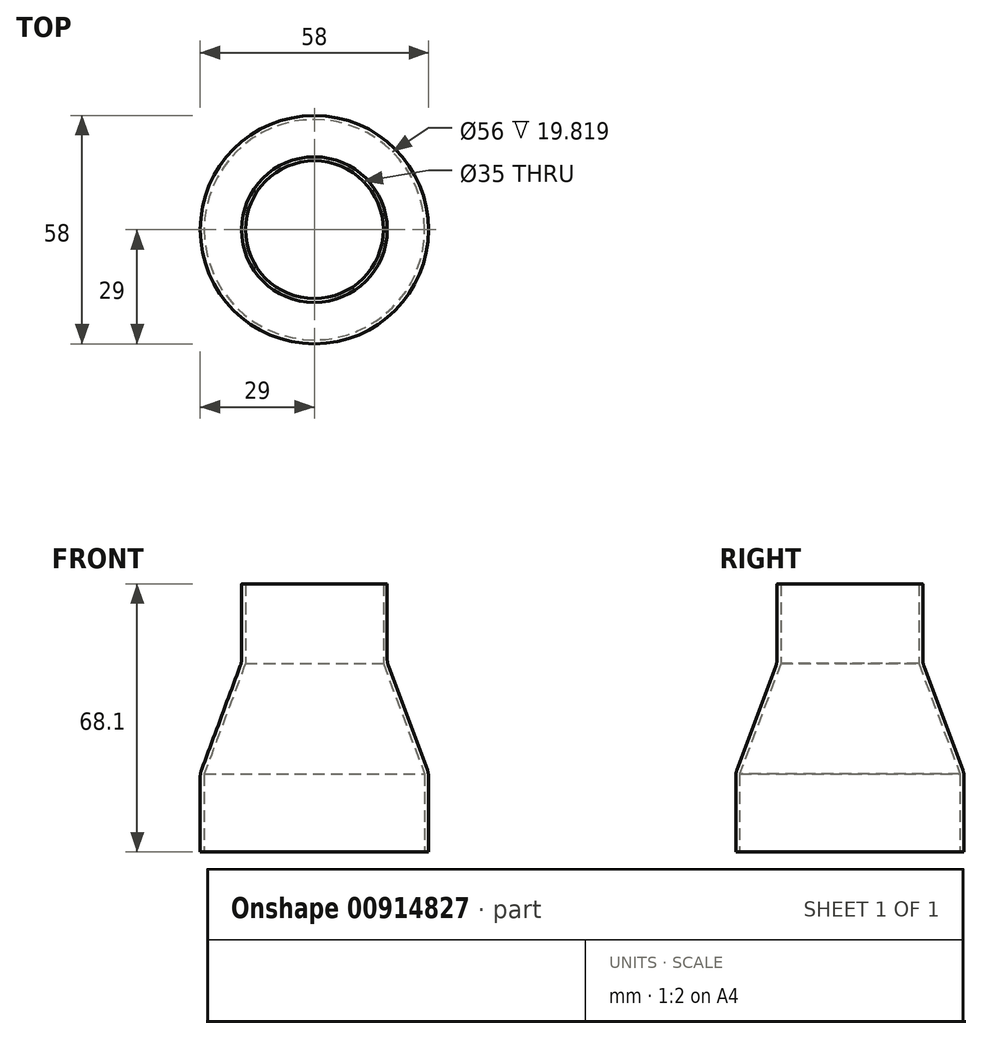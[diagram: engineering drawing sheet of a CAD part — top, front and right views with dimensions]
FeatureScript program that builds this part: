
annotation { "Feature Type Name" : "Feature", "Feature Type Description" : "" }
export const myFeature = defineFeature(function(context is Context, id is Id, definition is map)
    precondition{}
    {
        {
            var Q0;
            Q0=qCreatedBy(makeId("Front.planeOp"),FACE);
            var sketch = newSketch(context, id + "F0", { "sketchPlane" : qUnion([Q0])});
            skLineSegment(sketch, "E0", {"start": v(-29, 0) * mm, "end": v(-29, 20) * mm});
            skLineSegment(sketch, "E1", {"start": v(-29, 20) * mm, "end": v(-18.5, 48.1) * mm});
            skLineSegment(sketch, "E2", {"start": v(-18.5, 48.1) * mm, "end": v(-18.5, 68.1) * mm});
            skLineSegment(sketch, "E3.0", {"start": v(-17.5, 47.92) * mm, "end": v(-17.5, 68.1) * mm});
            skLineSegment(sketch, "E3.1", {"start": v(-28, 19.82) * mm, "end": v(-17.5, 47.92) * mm});
            skLineSegment(sketch, "E3.2", {"start": v(-28, 0) * mm, "end": v(-28, 19.82) * mm});
            skLineSegment(sketch, "E4", {"start": v(-29, 0) * mm, "end": v(-28, 0) * mm});
            skLineSegment(sketch, "E5", {"start": v(-18.5, 68.1) * mm, "end": v(-17.5, 68.1) * mm});
            skLineSegment(sketch, "E6", {"start": v(0, 0) * mm, "end": v(0, 46.9) * mm, "construction": true});
            skSolve(sketch);
        }
        {
            var Q0;
            Q0=makeQuery(id+"F0.imprint","IMPRINT",FACE,{"disambiguationData":[TD([[makeQuery(id+"F0.imprint","IMPRINT",EDGE,{"derivedFrom":sQuery(id+"F0.wireOp",EDGE,"E0")}),-1.0]])]});
            var Q1;
            Q1=sQuery(id+"F0.wireOp",EDGE,"E6");
            revolve(context, id + "F1", {"entities" : qUnion([Q0]), "axis" : qUnion([Q1]), "revolveType" : RevolveType.FULL});
        }
        {
            var Q0;
            Q0=makeQuery(id+"F1.opRevolve","SWEPT_EDGE",EDGE,{"disambiguationData":[OSD([sQuery(id+"F0.wireOp",EDGE,"E0"),sQuery(id+"F0.wireOp",EDGE,"E1")])]});
            var Q1;
            {var subQ0=sQuery(id+"FaZu06GFXP2sTeX_1.wireOp",EDGE,"TdJHtMkF-AUQf-TWFz-uHxR-ayQx0xFrAdBq");Q1=makeQuery(id+"FlHbGjVHjVcW52T_2.opFillet","BLEND_EDGE",EDGE,{"blendedFrom":[makeQuery(id+"FhDor8GWW6OAFC3_1.opExtrude","CAP_EDGE",EDGE,{"disambiguationData":[OSD([subQ0])],"isStart":true}),makeQuery(id+"FhDor8GWW6OAFC3_1.opExtrude","CAP_FACE",FACE,{"disambiguationData":[OSD([sQuery(id+"FaZu06GFXP2sTeX_1.wireOp",EDGE,"fHvzw86X-V8rq-VAlk-hoMZ-7mlJtmEaRwba.bottom"),sQuery(id+"FaZu06GFXP2sTeX_1.wireOp",EDGE,"fHvzw86X-V8rq-VAlk-hoMZ-7mlJtmEaRwba.top"),sQuery(id+"FaZu06GFXP2sTeX_1.wireOp",EDGE,"fHvzw86X-V8rq-VAlk-hoMZ-7mlJtmEaRwba.left"),sQuery(id+"FaZu06GFXP2sTeX_1.wireOp",EDGE,"fHvzw86X-V8rq-VAlk-hoMZ-7mlJtmEaRwba.right"),subQ0])],"isStart":true})],"blendedInto":[makeQuery(id+"FhDor8GWW6OAFC3_1.opExtrude","CAP_FACE",FACE,{"disambiguationData":[OSD([sQuery(id+"FaZu06GFXP2sTeX_1.wireOp",EDGE,"fHvzw86X-V8rq-VAlk-hoMZ-7mlJtmEaRwba.bottom"),sQuery(id+"FaZu06GFXP2sTeX_1.wireOp",EDGE,"fHvzw86X-V8rq-VAlk-hoMZ-7mlJtmEaRwba.top"),sQuery(id+"FaZu06GFXP2sTeX_1.wireOp",EDGE,"fHvzw86X-V8rq-VAlk-hoMZ-7mlJtmEaRwba.left"),sQuery(id+"FaZu06GFXP2sTeX_1.wireOp",EDGE,"fHvzw86X-V8rq-VAlk-hoMZ-7mlJtmEaRwba.right"),subQ0])],"isStart":true})]});}
            var Q2;
            Q2=makeQuery(id+"F1.opRevolve","SWEPT_EDGE",EDGE,{"disambiguationData":[OSD([sQuery(id+"F0.wireOp",EDGE,"E1"),sQuery(id+"F0.wireOp",EDGE,"E2")])]});
            fillet(context, id + "F2", {"entities" : qUnion([Q0, Q1, Q2]), "radius" : 5 * mm, "tangentPropagation" : true, "allowEdgeOverflow" : false});
        }
        {
            var Q0;
            Q0=makeQuery(id+"F1.opRevolve","SWEPT_FACE",FACE,{"disambiguationData":[OSD([sQuery(id+"F0.wireOp",EDGE,"E5")])]});
            fillet(context, id + "F3", {"entities" : qUnion([Q0]), "radius" : .1 * mm, "tangentPropagation" : true, "allowEdgeOverflow" : false});
        }
    });
